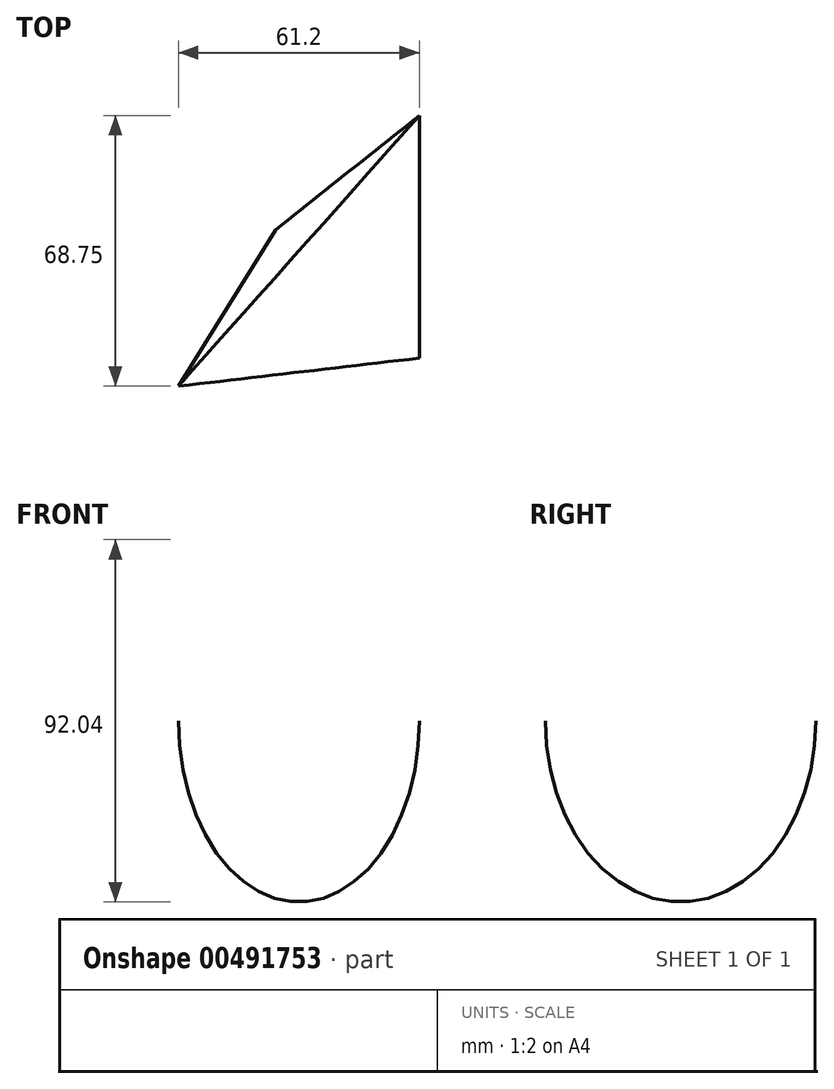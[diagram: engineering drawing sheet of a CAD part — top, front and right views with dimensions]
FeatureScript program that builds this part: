
annotation { "Feature Type Name" : "Feature", "Feature Type Description" : "" }
export const myFeature = defineFeature(function(context is Context, id is Id, definition is map)
    precondition{}
    {
        {
            var Q0;
            Q0=qCreatedBy(makeId("Top.planeOp"),FACE);
            var sketch = newSketch(context, id + "F0", { "sketchPlane" : qUnion([Q0])});
            skLineSegment(sketch, "E0", {"start": v(0, 0) * mm, "end": v(36.56, -32.55) * mm});
            skLineSegment(sketch, "E1", {"start": v(36.56, -32.55) * mm, "end": v(36.56, 29.07) * mm});
            skLineSegment(sketch, "E2", {"start": v(36.56, 29.07) * mm, "end": v(0, 0) * mm});
            skSolve(sketch);
        }
        {
            var Q0;
            Q0=makeQuery(id+"F0.imprint","IMPRINT",FACE,{"disambiguationData":[TD([[makeQuery(id+"F0.imprint","IMPRINT",EDGE,{"derivedFrom":sQuery(id+"F0.wireOp",EDGE,"E0")}),1.0]])]});
            var Q1;
            Q1=sQuery(id+"F0.wireOp",EDGE,"E0");
            revolve(context, id + "F1", {"entities" : qUnion([Q0]), "axis" : qUnion([Q1]), "revolveType" : RevolveType.FULL});
        }
    });
